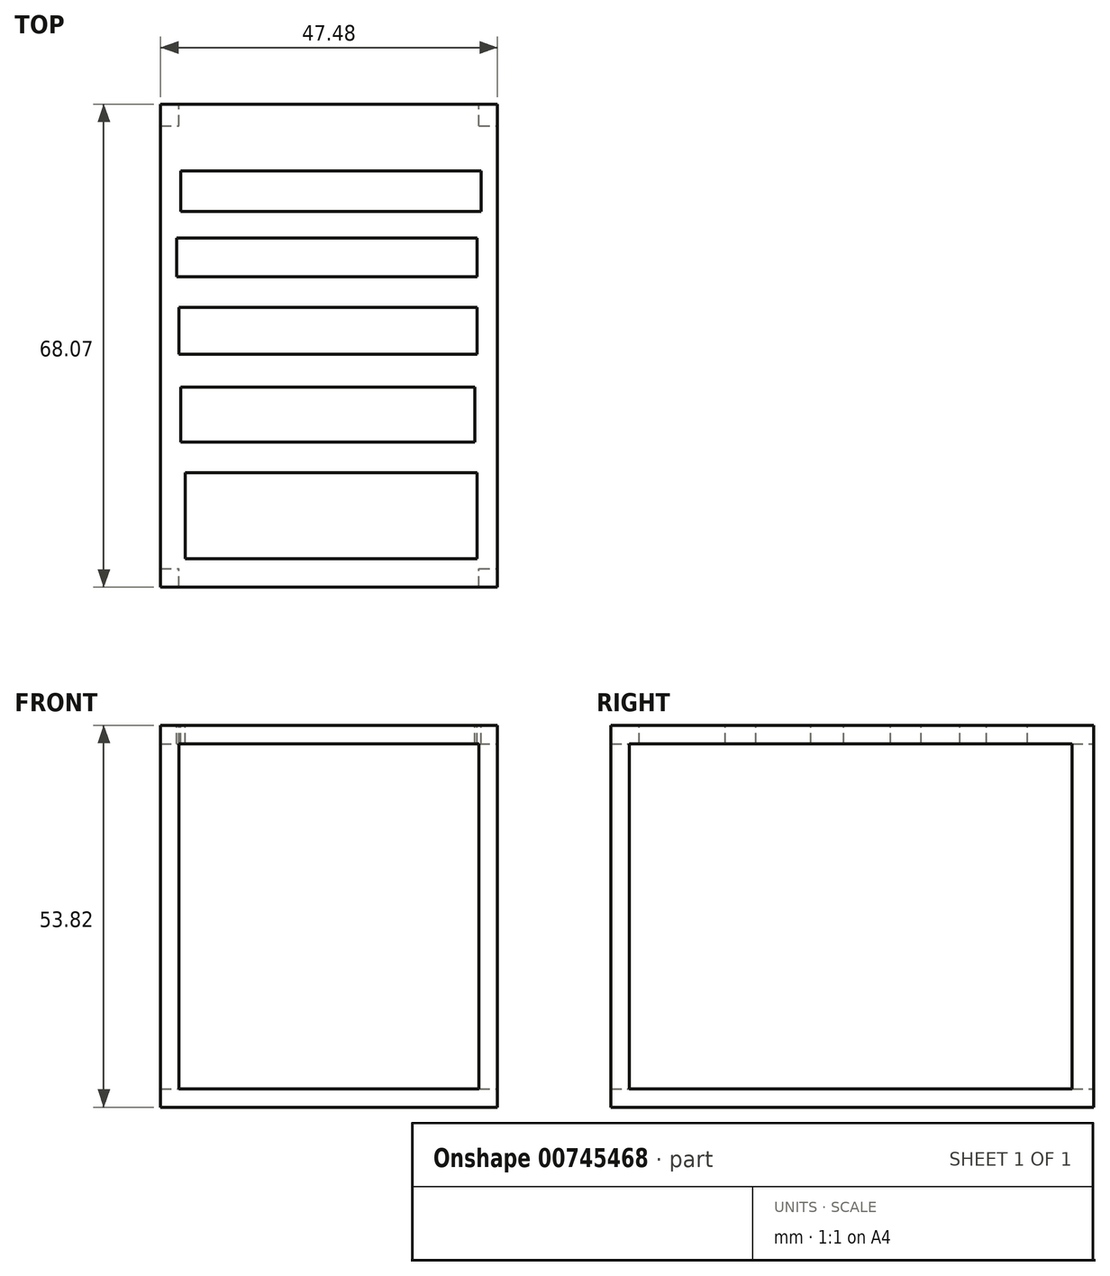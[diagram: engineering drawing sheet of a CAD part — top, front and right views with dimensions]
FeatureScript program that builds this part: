
annotation { "Feature Type Name" : "Feature", "Feature Type Description" : "" }
export const myFeature = defineFeature(function(context is Context, id is Id, definition is map)
    precondition{}
    {
        {
            var Q0;
            Q0=qCreatedBy(makeId("Front.planeOp"),FACE);
            var sketch = newSketch(context, id + "F0", { "sketchPlane" : qUnion([Q0])});
            skLineSegment(sketch, "E0.bottom", {"start": v(-23.74, -26.9) * mm, "end": v(23.74, -26.9) * mm});
            skLineSegment(sketch, "E0.top", {"start": v(-23.74, 26.9) * mm, "end": v(23.74, 26.9) * mm});
            skLineSegment(sketch, "E0.left", {"start": v(-23.74, -26.9) * mm, "end": v(-23.74, 26.9) * mm});
            skLineSegment(sketch, "E0.right", {"start": v(23.74, -26.9) * mm, "end": v(23.74, 26.9) * mm});
            skPoint(sketch, "E0.middle", {"position": v(0, 0) * mm});
            skLineSegment(sketch, "E1.bottom", {"start": v(-21.15, -24.32) * mm, "end": v(21.15, -24.32) * mm});
            skLineSegment(sketch, "E1.top", {"start": v(-21.15, 24.32) * mm, "end": v(21.15, 24.32) * mm});
            skLineSegment(sketch, "E1.left", {"start": v(-21.15, -24.32) * mm, "end": v(-21.15, 24.32) * mm});
            skLineSegment(sketch, "E1.right", {"start": v(21.15, -24.32) * mm, "end": v(21.15, 24.32) * mm});
            skSolve(sketch);
        }
        {
            var Q0;
            Q0 = qSketchRegion(id + "F0", true);
            extrude(context, id + "F1", {"entities" : qUnion([Q0]), "depth" : 68.07 * mm, "offsetDistance" : 25.4 * mm});
        }
        {
            var Q0;
            Q0=makeQuery(id+"F1.opExtrude","SWEPT_FACE",FACE,{"disambiguationData":[OSD([sQuery(id+"F0.wireOp",EDGE,"E0.right")])]});
            var sketch = newSketch(context, id + "F2", { "sketchPlane" : qUnion([Q0])});
            skLineSegment(sketch, "E2.bottom", {"start": v(-3.02, 24.32) * mm, "end": v(-65.48, 24.32) * mm});
            skLineSegment(sketch, "E2.top", {"start": v(-3.02, -24.32) * mm, "end": v(-65.48, -24.32) * mm});
            skLineSegment(sketch, "E2.left", {"start": v(-3.02, 24.32) * mm, "end": v(-3.02, -24.32) * mm});
            skLineSegment(sketch, "E2.right", {"start": v(-65.48, 24.32) * mm, "end": v(-65.48, -24.32) * mm});
            skSolve(sketch);
        }
        {
            var Q0;
            Q0=makeQuery(id+"F2.imprint","IMPRINT",FACE,{"disambiguationData":[TD([[makeQuery(id+"F2.imprint","IMPRINT",EDGE,{"derivedFrom":sQuery(id+"F2.wireOp",EDGE,"E2.bottom")}),1.0]])]});
            extrude(context, id + "F3", {"entities" : qUnion([Q0]), "operationType" : NewBodyOperationType.REMOVE, "oppositeDirection" : true, "depth" : 68.07 * mm, "offsetDistance" : 25.4 * mm});
        }
        {
            var Q0;
            Q0=makeQuery(id+"F1.opExtrude","SWEPT_FACE",FACE,{"disambiguationData":[OSD([sQuery(id+"F0.wireOp",EDGE,"E0.top")])]});
            var sketch = newSketch(context, id + "F4", { "sketchPlane" : qUnion([Q0])});
            skLineSegment(sketch, "E3.bottom", {"start": v(-20.3, -64.05) * mm, "end": v(20.85, -64.05) * mm});
            skLineSegment(sketch, "E3.top", {"start": v(-20.3, -51.96) * mm, "end": v(20.85, -51.96) * mm});
            skLineSegment(sketch, "E3.left", {"start": v(-20.3, -64.05) * mm, "end": v(-20.3, -51.96) * mm});
            skLineSegment(sketch, "E3.right", {"start": v(20.85, -64.05) * mm, "end": v(20.85, -51.96) * mm});
            skLineSegment(sketch, "E4.bottom", {"start": v(-20.88, -47.65) * mm, "end": v(20.56, -47.65) * mm});
            skLineSegment(sketch, "E4.top", {"start": v(-20.88, -39.88) * mm, "end": v(20.56, -39.88) * mm});
            skLineSegment(sketch, "E4.left", {"start": v(-20.88, -47.65) * mm, "end": v(-20.88, -39.88) * mm});
            skLineSegment(sketch, "E4.right", {"start": v(20.56, -47.65) * mm, "end": v(20.56, -39.88) * mm});
            skLineSegment(sketch, "E5.bottom", {"start": v(-21.17, -35.27) * mm, "end": v(20.85, -35.27) * mm});
            skLineSegment(sketch, "E5.top", {"start": v(-21.17, -28.65) * mm, "end": v(20.85, -28.65) * mm});
            skLineSegment(sketch, "E5.left", {"start": v(-21.17, -35.27) * mm, "end": v(-21.17, -28.65) * mm});
            skLineSegment(sketch, "E5.right", {"start": v(20.85, -35.27) * mm, "end": v(20.85, -28.65) * mm});
            skLineSegment(sketch, "E6.bottom", {"start": v(-21.46, -24.33) * mm, "end": v(20.85, -24.33) * mm});
            skLineSegment(sketch, "E6.top", {"start": v(-21.46, -18.87) * mm, "end": v(20.85, -18.87) * mm});
            skLineSegment(sketch, "E6.left", {"start": v(-21.46, -24.33) * mm, "end": v(-21.46, -18.87) * mm});
            skLineSegment(sketch, "E6.right", {"start": v(20.85, -24.33) * mm, "end": v(20.85, -18.87) * mm});
            skLineSegment(sketch, "E7.bottom", {"start": v(-20.88, -9.37) * mm, "end": v(21.43, -9.37) * mm});
            skLineSegment(sketch, "E7.top", {"start": v(-20.88, -15.12) * mm, "end": v(21.43, -15.12) * mm});
            skLineSegment(sketch, "E7.left", {"start": v(-20.88, -9.37) * mm, "end": v(-20.88, -15.12) * mm});
            skLineSegment(sketch, "E7.right", {"start": v(21.43, -9.37) * mm, "end": v(21.43, -15.12) * mm});
            skSolve(sketch);
        }
        {
            var Q0;
            Q0 = qSketchRegion(id + "F4", true);
            extrude(context, id + "F5", {"entities" : qUnion([Q0]), "operationType" : NewBodyOperationType.REMOVE, "oppositeDirection" : true, "depth" : 25.4 * mm, "offsetDistance" : 25.4 * mm});
        }
    });
